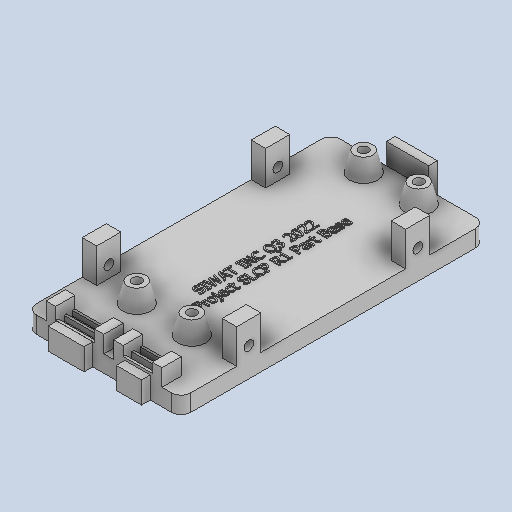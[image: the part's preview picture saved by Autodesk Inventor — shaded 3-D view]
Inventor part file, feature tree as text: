
AUTODESK INVENTOR PART (.ipt)
format: ipt  version: 2023 (Build 270158000, 158)  size: 1,408,000 bytes
history: native  units: in
note: dims shown in document units (in); Inventor stores cm internally (conversion verified against a paired STEP export)
features: extrude x13, sketch x13, projected_geometry x11, other x4, reference x3, plane x2, chamfer x1
ambient origin geometry x8: Origin, YZ Plane, XZ Plane, XY Plane, X Axis, Y Axis, Z Axis, Center Point
bodies: Solid1 (feature_tree)
feature tree (47):
  extrude  "Extrusion1"  Depth=0.0197in
  extrude  "Extrusion2"  Depth=0.0197in
  chamfer  "Chamfer1"  Distance=0.1378in
  extrude  "Extrusion3"  Depth=0.0591in
  extrude  "Extrusion4"  Depth=0.0591in
  extrude  "Extrusion5"  Depth=0.0787in
  extrude  "Extrusion6"  Depth=0.0787in
  extrude  "Extrusion7"  Depth=0.1575in TaperAngle=0.0deg
  sketch  "Sketch8"  dims[d12=0.0591in d13=0.0591in]
  plane  "Work Plane1"
  extrude  "Extrusion8"  Depth=0.1181in
  extrude  "Extrusion9"  Depth=0.1181in
  sketch  "Sketch11"  dims[d16=0.0787in d17=0.0787in]
  plane  "Work Plane2"
  extrude  "Extrusion10"  Depth=0.1969in
  extrude  "Extrusion11"  Depth=0.1181in
  extrude  "Extrusion12"  Depth=0.1969in
  extrude  "Extrusion13"  Depth=0.1181in
  sketch  "Sketch1"  dims[d0=0.0197in d1=0.0197in]
  reference  "Reference1"
  sketch  "Sketch2"  dims[d2=0.0197in d3=0.0197in]
  reference  "Reference2"
  sketch  "Sketch3"  dims[d4=0.0394in]
  sketch  "Sketch4"  dims[d5=0.1969in]
  sketch  "Sketch5"  dims[d6=0.1969in]
  sketch  "Sketch6"  dims[d7=0.3937in d8=0.1378in d9=0.0in]
  sketch  "Sketch7"  dims[d10=0.0787in d11=0.0591in]
  reference  "Reference3"
  sketch  "Sketch10"  dims[d14=0.0591in d15=0.0787in]
  projected_geometry  "Projected Loop1"
  projected_geometry  "Projected Loop2"
  projected_geometry  "Projected Loop3"
  projected_geometry  "Projected Loop4"
  sketch  "Sketch12"  dims[d18=0.0787in d19=0.1575in d20=0.0in]
  projected_geometry  "Projected Loop5"
  projected_geometry  "Projected Loop6"
  projected_geometry  "Projected Loop7"
  projected_geometry  "Projected Loop8"
  sketch  "Sketch13"  dims[d21=0.0394in d22=0.1575in d23=45.0deg d27=0.1181in]
  projected_geometry  "Projected Loop9"
  projected_geometry  "Projected Loop10"
  projected_geometry  "Projected Loop11"
  sketch  "Sketch14"  dims[d28=0.1969in d29=0.1181in d30=0.1969in d31=0.1181in d32=0.1969in d33=0.1181in d34=0.1969in d35=1.1811in d36=2.4803in d37=0.4528in d38=0.1969in d39=0.0in d40=0.0787in d41=0.0984in d42=0.0787in d43=0.0984in d44=1.5719in d45=0.0in d46=0.3937in d47=0.0in d48=0.315in d49=0.1575in d50=0.2362in d51=0.1575in d52=0.0787in d53=0.0787in d54=0.0787in d55=0.0787in d56=0.1575in d57=0.1575in d58=0.1378in d59=0.0in d60=0.0197in d61=0.0197in d62=0.0098in d63=0.0098in d64=0.0098in d65=0.0098in d66=0.0591in d67=0.0in d68=0.0753in d69=0.0in d70=0.1772in d71=0.0in d78=0.0827in d79=0.0in d80=0.0118in d81=0.0118in d82=0.0118in d83=0.0118in d84=0.126in d85=0.0in d86=0.0187in d87=0.0in d88=0.0079in d89=0.0in d72=0.0197in d73=0.0344in]
  parser-record x1  (decoder bookkeeping rows leaked as tree rows — omitted from the tree; the rows remain in map.json)
  other  "Casing.iam"
  other  "Raspberry Pi Pico-R3:1"
  other  "cover:1"
note: 1 file-system path scrubbed to <path> (originals preserved in map.json)
